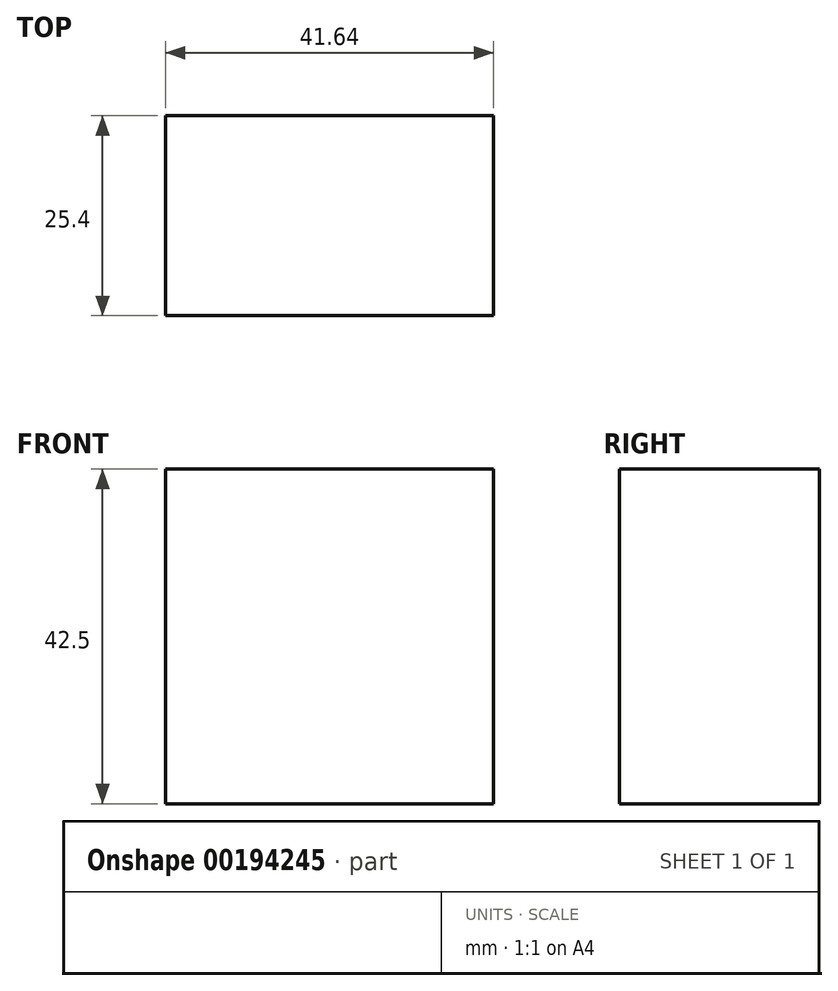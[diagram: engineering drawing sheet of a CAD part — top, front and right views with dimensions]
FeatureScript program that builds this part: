
annotation { "Feature Type Name" : "Feature", "Feature Type Description" : "" }
export const myFeature = defineFeature(function(context is Context, id is Id, definition is map)
    precondition{}
    {
        {
            var Q0;
            Q0=qCreatedBy(makeId("Front.planeOp"),FACE);
            var sketch = newSketch(context, id + "F0", { "sketchPlane" : qUnion([Q0])});
            skLineSegment(sketch, "E0.bottom", {"start": v(-20.82, 21.25) * mm, "end": v(20.82, 21.25) * mm});
            skLineSegment(sketch, "E0.top", {"start": v(-20.82, -21.25) * mm, "end": v(20.82, -21.25) * mm});
            skLineSegment(sketch, "E0.left", {"start": v(-20.82, 21.25) * mm, "end": v(-20.82, -21.25) * mm});
            skLineSegment(sketch, "E0.right", {"start": v(20.82, 21.25) * mm, "end": v(20.82, -21.25) * mm});
            skPoint(sketch, "E0.middle", {"position": v(0, 0) * mm});
            skSolve(sketch);
        }
        {
            var Q0;
            Q0=makeQuery(id+"F0.imprint","IMPRINT",FACE,{"disambiguationData":[TD([[makeQuery(id+"F0.imprint","IMPRINT",EDGE,{"derivedFrom":sQuery(id+"F0.wireOp",EDGE,"E0.bottom")}),-1.0]])]});
            extrude(context, id + "F1", {"entities" : qUnion([Q0]), "depth" : 25.4 * mm});
        }
    });
